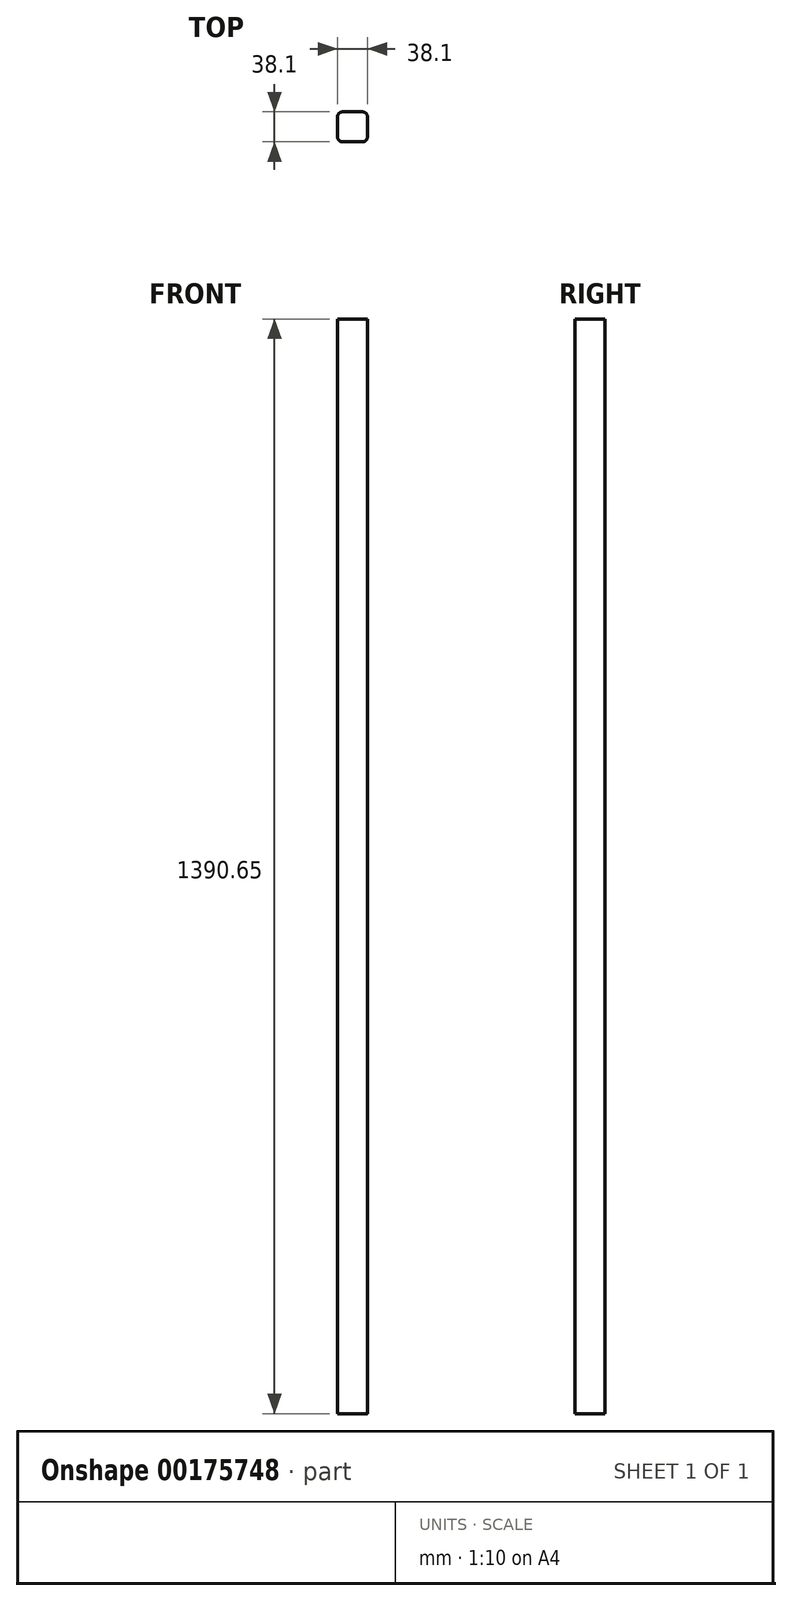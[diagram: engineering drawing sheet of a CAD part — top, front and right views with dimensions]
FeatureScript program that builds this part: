
annotation { "Feature Type Name" : "Feature", "Feature Type Description" : "" }
export const myFeature = defineFeature(function(context is Context, id is Id, definition is map)
    precondition{}
    {
        {
            var Q0;
            Q0=qCreatedBy(makeId("Top.planeOp"),FACE);
            var sketch = newSketch(context, id + "F0", { "sketchPlane" : qUnion([Q0])});
            skLineSegment(sketch, "E0.bottom", {"start": v(12.7, 19.05) * mm, "end": v(-12.7, 19.05) * mm});
            skLineSegment(sketch, "E0.top", {"start": v(12.7, -19.05) * mm, "end": v(-12.7, -19.05) * mm});
            skLineSegment(sketch, "E0.left", {"start": v(19.05, 12.7) * mm, "end": v(19.05, -12.7) * mm});
            skLineSegment(sketch, "E0.right", {"start": v(-19.05, 12.7) * mm, "end": v(-19.05, -12.7) * mm});
            skPoint(sketch, "E0.middle", {"position": v(0, 0) * mm});
            skPoint(sketch, "E1.visualSharp", {"position": v(-19.05, 19.05) * mm});
            skArc(sketch, "E1.filletArc", {"start": v(-12.7, 19.05) * mm, "mid": v(-17.2, 17.2) * mm, "end": v(-19.05, 12.7) * mm});
            skPoint(sketch, "E2.visualSharp", {"position": v(19.05, 19.05) * mm});
            skArc(sketch, "E2.filletArc", {"start": v(19.05, 12.7) * mm, "mid": v(17.2, 17.2) * mm, "end": v(12.7, 19.05) * mm});
            skPoint(sketch, "E3.visualSharp", {"position": v(19.05, -19.05) * mm});
            skArc(sketch, "E3.filletArc", {"start": v(12.7, -19.05) * mm, "mid": v(17.2, -17.2) * mm, "end": v(19.05, -12.7) * mm});
            skPoint(sketch, "E4.visualSharp", {"position": v(-19.05, -19.05) * mm});
            skArc(sketch, "E4.filletArc", {"start": v(-19.05, -12.7) * mm, "mid": v(-17.2, -17.2) * mm, "end": v(-12.7, -19.05) * mm});
            skSolve(sketch);
        }
        {
            var Q0;
            Q0 = qSketchRegion(id + "F0", true);
            extrude(context, id + "F1", {"entities" : qUnion([Q0]), "depth" : 1390.65 * mm});
        }
    });
